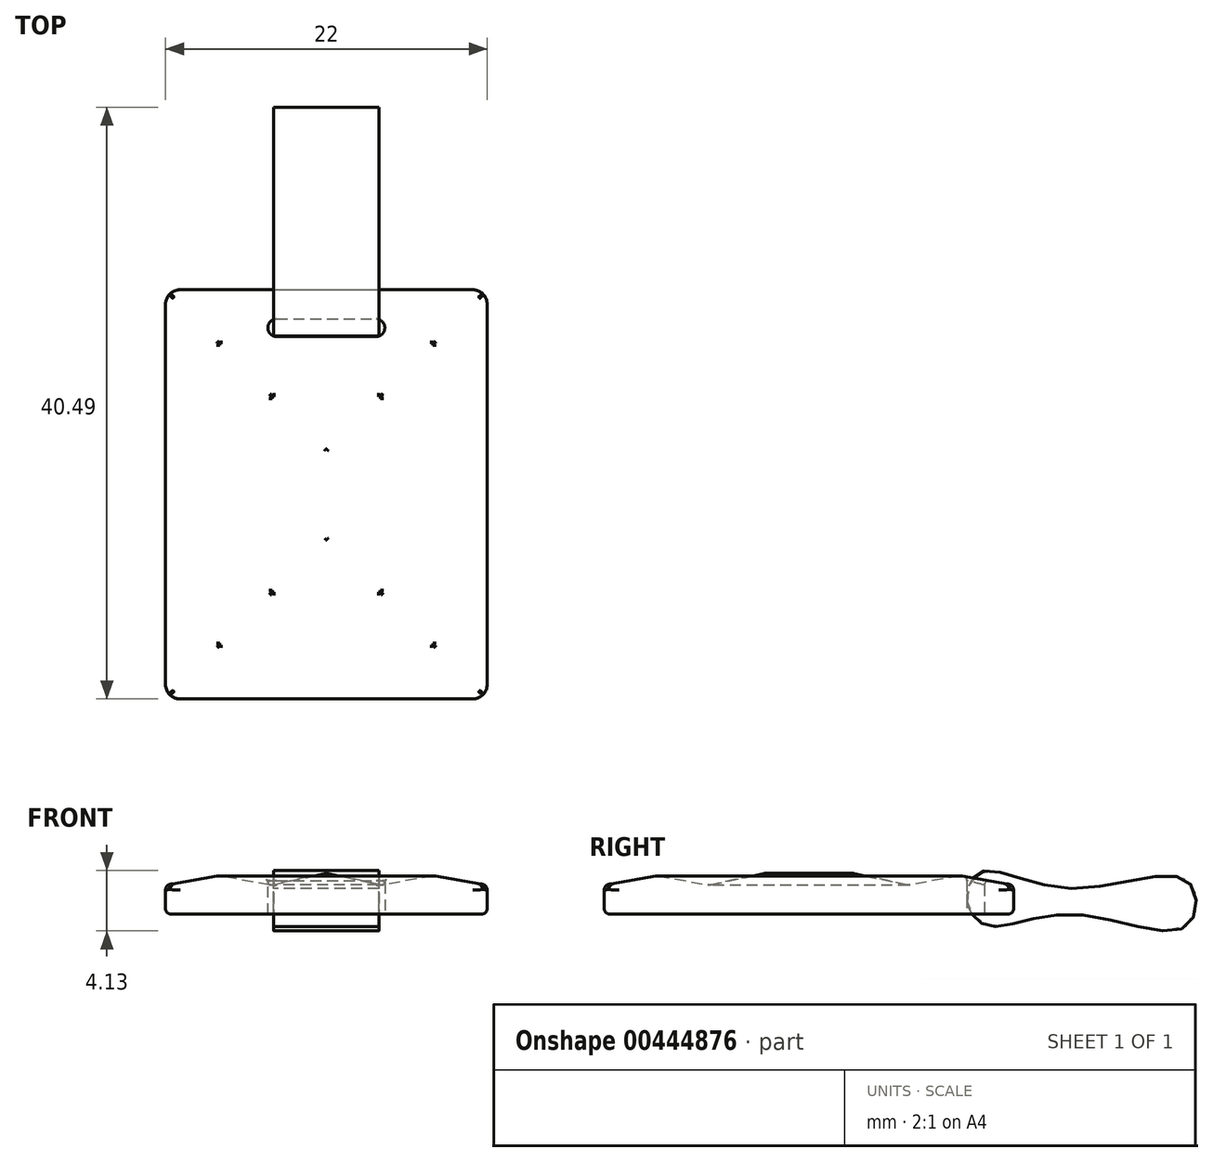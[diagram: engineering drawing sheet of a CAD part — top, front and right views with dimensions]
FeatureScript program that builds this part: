
annotation { "Feature Type Name" : "Feature", "Feature Type Description" : "" }
export const myFeature = defineFeature(function(context is Context, id is Id, definition is map)
    precondition{}
    {
        {
            var Q0;
            Q0=qCreatedBy(makeId("Top.planeOp"),FACE);
            var sketch = newSketch(context, id + "F0", { "sketchPlane" : qUnion([Q0])});
            skLineSegment(sketch, "E0.bottom", {"start": v(-11, 14) * mm, "end": v(11, 14) * mm});
            skLineSegment(sketch, "E0.top", {"start": v(-11, -14) * mm, "end": v(11, -14) * mm});
            skLineSegment(sketch, "E0.left", {"start": v(-11, 14) * mm, "end": v(-11, -14) * mm});
            skLineSegment(sketch, "E0.right", {"start": v(11, 14) * mm, "end": v(11, -14) * mm});
            skPoint(sketch, "E0.middle", {"position": v(0, 0) * mm});
            skSolve(sketch);
        }
        {
            var Q0;
            Q0 = qSketchRegion(id + "F0", true);
            extrude(context, id + "F1", {"entities" : qUnion([Q0]), "depth" : 2 * mm});
        }
        {
            var Q0;
            Q0=makeQuery(id+"F1.opExtrude","CAP_FACE",FACE,{"disambiguationData":[OSD([sQuery(id+"F0.wireOp",EDGE,"E0.bottom"),sQuery(id+"F0.wireOp",EDGE,"E0.top"),sQuery(id+"F0.wireOp",EDGE,"E0.left"),sQuery(id+"F0.wireOp",EDGE,"E0.right")])],"isStart":false});
            var sketch = newSketch(context, id + "F2", { "sketchPlane" : qUnion([Q0])});
            skLineSegment(sketch, "E1.bottom", {"start": v(-3.8, 6.8) * mm, "end": v(3.8, 6.8) * mm});
            skLineSegment(sketch, "E1.top", {"start": v(-3.8, -6.8) * mm, "end": v(3.8, -6.8) * mm});
            skLineSegment(sketch, "E1.left", {"start": v(-3.8, 6.8) * mm, "end": v(-3.8, -6.8) * mm});
            skLineSegment(sketch, "E1.right", {"start": v(3.8, 6.8) * mm, "end": v(3.8, -6.8) * mm});
            skPoint(sketch, "E1.middle", {"position": v(0, 0) * mm});
            skSolve(sketch);
        }
        {
            var Q0;
            Q0=makeQuery(id+"F2.imprint","IMPRINT",FACE,{"disambiguationData":[TD([[makeQuery(id+"F2.imprint","IMPRINT",EDGE,{"derivedFrom":sQuery(id+"F2.wireOp",EDGE,"E1.bottom")}),1.0]])]});
            extrude(context, id + "F3", {"entities" : qUnion([Q0]), "operationType" : NewBodyOperationType.ADD, "depth" : 25 * mm, "hasDraft" : true, "draftAngle" : 80 * degree, "draftPullDirection" : true});
        }
        {
            var Q0;
            Q0=makeQuery(id+"F1.opExtrude","CAP_FACE",FACE,{"disambiguationData":[OSD([sQuery(id+"F0.wireOp",EDGE,"E0.bottom"),sQuery(id+"F0.wireOp",EDGE,"E0.top"),sQuery(id+"F0.wireOp",EDGE,"E0.left"),sQuery(id+"F0.wireOp",EDGE,"E0.right")])],"isStart":false});
            extrude(context, id + "F4", {"entities" : qUnion([Q0]), "operationType" : NewBodyOperationType.ADD, "depth" : 25 * mm, "hasDraft" : true, "draftAngle" : 78 * degree, "draftPullDirection" : true});
        }
        {
            var Q0;
            Q0=makeQuery(id+"F1.opExtrude","SWEPT_EDGE",EDGE,{"disambiguationData":[OSD([sQuery(id+"F0.wireOp",EDGE,"E0.bottom"),sQuery(id+"F0.wireOp",EDGE,"E0.left")])]});
            var Q1;
            Q1=makeQuery(id+"F1.opExtrude","SWEPT_EDGE",EDGE,{"disambiguationData":[OSD([sQuery(id+"F0.wireOp",EDGE,"E0.top"),sQuery(id+"F0.wireOp",EDGE,"E0.left")])]});
            var Q2;
            Q2=makeQuery(id+"F1.opExtrude","SWEPT_EDGE",EDGE,{"disambiguationData":[OSD([sQuery(id+"F0.wireOp",EDGE,"E0.top"),sQuery(id+"F0.wireOp",EDGE,"E0.right")])]});
            var Q3;
            Q3=makeQuery(id+"F1.opExtrude","SWEPT_EDGE",EDGE,{"disambiguationData":[OSD([sQuery(id+"F0.wireOp",EDGE,"E0.bottom"),sQuery(id+"F0.wireOp",EDGE,"E0.right")])]});
            fillet(context, id + "F5", {"entities" : qUnion([Q0, Q1, Q2, Q3]), "radius" : 1 * mm, "tangentPropagation" : true, "allowEdgeOverflow" : false});
        }
        {
            var Q0;
            Q0=makeQuery(id+"F3.opExtrude","SWEPT_EDGE",EDGE,{"disambiguationData":[OSD([sQuery(id+"F0.wireOp",EDGE,"E0.bottom"),sQuery(id+"F0.wireOp",EDGE,"E0.left")])]});
            var Q1;
            Q1=makeQuery(id+"F3.opExtrude","SWEPT_EDGE",EDGE,{"disambiguationData":[OSD([sQuery(id+"F2.wireOp",EDGE,"E1.bottom"),sQuery(id+"F2.wireOp",EDGE,"E1.left")])]});
            var Q2;
            Q2=makeQuery(id+"F4.opExtrude","SWEPT_EDGE",EDGE,{"disambiguationData":[OSD([sQuery(id+"F2.wireOp",EDGE,"E1.bottom"),sQuery(id+"F2.wireOp",EDGE,"E1.left")])]});
            var Q3;
            Q3=makeQuery(id+"F4.opExtrude","SWEPT_EDGE",EDGE,{"disambiguationData":[OSD([sQuery(id+"F2.wireOp",EDGE,"E1.top"),sQuery(id+"F2.wireOp",EDGE,"E1.right")])]});
            var Q4;
            Q4=makeQuery(id+"F3.opExtrude","SWEPT_EDGE",EDGE,{"disambiguationData":[OSD([sQuery(id+"F2.wireOp",EDGE,"E1.top"),sQuery(id+"F2.wireOp",EDGE,"E1.right")])]});
            var Q5;
            Q5=makeQuery(id+"F3.opExtrude","SWEPT_EDGE",EDGE,{"disambiguationData":[OSD([sQuery(id+"F0.wireOp",EDGE,"E0.top"),sQuery(id+"F0.wireOp",EDGE,"E0.right")])]});
            var Q6;
            Q6=makeQuery(id+"F4.opExtrude","SWEPT_EDGE",EDGE,{"disambiguationData":[OSD([sQuery(id+"F2.wireOp",EDGE,"E1.top"),sQuery(id+"F2.wireOp",EDGE,"E1.left")])]});
            var Q7;
            Q7=makeQuery(id+"F4.opExtrude","SWEPT_EDGE",EDGE,{"disambiguationData":[OSD([sQuery(id+"F2.wireOp",EDGE,"E1.bottom"),sQuery(id+"F2.wireOp",EDGE,"E1.right")])]});
            var Q8;
            Q8=makeQuery(id+"F3.opExtrude","SWEPT_EDGE",EDGE,{"disambiguationData":[OSD([sQuery(id+"F2.wireOp",EDGE,"E1.top"),sQuery(id+"F2.wireOp",EDGE,"E1.left")])]});
            var Q9;
            Q9=makeQuery(id+"F3.opExtrude","SWEPT_EDGE",EDGE,{"disambiguationData":[OSD([sQuery(id+"F0.wireOp",EDGE,"E0.top"),sQuery(id+"F0.wireOp",EDGE,"E0.left")])]});
            var Q10;
            Q10=makeQuery(id+"F3.opExtrude","SWEPT_EDGE",EDGE,{"disambiguationData":[OSD([sQuery(id+"F2.wireOp",EDGE,"E1.bottom"),sQuery(id+"F2.wireOp",EDGE,"E1.right")])]});
            var Q11;
            Q11=makeQuery(id+"F3.opExtrude","SWEPT_EDGE",EDGE,{"disambiguationData":[OSD([sQuery(id+"F0.wireOp",EDGE,"E0.bottom"),sQuery(id+"F0.wireOp",EDGE,"E0.right")])]});
            fillet(context, id + "F6", {"entities" : qUnion([Q0, Q1, Q2, Q3, Q4, Q5, Q6, Q7, Q8, Q9, Q10, Q11]), "radius" : 0.6 * mm, "tangentPropagation" : true, "allowEdgeOverflow" : false});
        }
        {
            var Q0;
            Q0=makeQuery(id+"F3.*.draft.opDraft","TWEAK_EDGE",EDGE,{"derivedFrom":[makeQuery(id+"F3.opExtrude","SWEPT_FACE",FACE,{"disambiguationData":[OSD([sQuery(id+"F2.wireOp",EDGE,"E1.bottom")])]}),makeQuery(id+"F3.opExtrude","SWEPT_FACE",FACE,{"disambiguationData":[OSD([sQuery(id+"F0.wireOp",EDGE,"E0.bottom")])]})]});
            var Q1;
            {var subQ0=sQuery(id+"F2.wireOp",EDGE,"E1.bottom");Q1=makeQuery(id+"F4.boolean.opBoolean","MERGE",EDGE,{"derivedFrom":[makeQuery(id+"F3.opExtrude","CAP_EDGE",EDGE,{"disambiguationData":[OSD([subQ0])],"isStart":true}),makeQuery(id+"F4.opExtrude","CAP_EDGE",EDGE,{"disambiguationData":[OSD([subQ0])],"isStart":true})]});}
            var Q2;
            Q2=makeQuery(id+"F4.*.draft.opDraft","TWEAK_EDGE",EDGE,{"derivedFrom":[makeQuery(id+"F4.opExtrude","SWEPT_FACE",FACE,{"disambiguationData":[OSD([sQuery(id+"F2.wireOp",EDGE,"E1.left")])]}),makeQuery(id+"F4.opExtrude","SWEPT_FACE",FACE,{"disambiguationData":[OSD([sQuery(id+"F2.wireOp",EDGE,"E1.right")])]})]});
            fillet(context, id + "F7", {"entities" : qUnion([Q0, Q1, Q2]), "radius" : 0.6 * mm, "tangentPropagation" : true, "allowEdgeOverflow" : false});
        }
        {
            var Q0;
            {var subQ0=sQuery(id+"F0.wireOp",EDGE,"E0.top");Q0=makeQuery(id+"F3.boolean.opBoolean","MERGE",EDGE,{"derivedFrom":[makeQuery(id+"F1.opExtrude","CAP_EDGE",EDGE,{"disambiguationData":[OSD([subQ0])],"isStart":false}),makeQuery(id+"F3.opExtrude","CAP_EDGE",EDGE,{"disambiguationData":[OSD([subQ0])],"isStart":true})]});}
            var Q1;
            Q1=makeQuery(id+"F1.opExtrude","CAP_EDGE",EDGE,{"disambiguationData":[OSD([sQuery(id+"F0.wireOp",EDGE,"E0.top")])],"isStart":true});
            fillet(context, id + "F8", {"entities" : qUnion([Q0, Q1]), "radius" : 0.4 * mm, "tangentPropagation" : true, "allowEdgeOverflow" : false});
        }
        {
            var Q0;
            Q0=qCreatedBy(makeId("Top.planeOp"),FACE);
            var sketch = newSketch(context, id + "F9", { "sketchPlane" : qUnion([Q0])});
            skLineSegment(sketch, "E2.bottom", {"start": v(-4, 10.8) * mm, "end": v(4, 10.8) * mm});
            skLineSegment(sketch, "E2.top", {"start": v(-4, 12) * mm, "end": v(4, 12) * mm});
            skLineSegment(sketch, "E2.left", {"start": v(-4, 10.8) * mm, "end": v(-4, 12) * mm});
            skLineSegment(sketch, "E2.right", {"start": v(4, 10.8) * mm, "end": v(4, 12) * mm});
            skPoint(sketch, "E2.middle", {"position": v(0, 11.4) * mm});
            skSolve(sketch);
        }
        {
            var Q0;
            Q0 = qSketchRegion(id + "F9", true);
            extrude(context, id + "F10", {"entities" : qUnion([Q0]), "operationType" : NewBodyOperationType.REMOVE, "depth" : 25 * mm});
        }
        {
            var Q0;
            Q0=makeQuery(id+"F10.boolean.opBoolean","COPY",EDGE,{"derivedFrom":makeQuery(id+"F10.opExtrude","SWEPT_EDGE",EDGE,{"disambiguationData":[OSD([sQuery(id+"F9.wireOp",EDGE,"E2.top"),sQuery(id+"F9.wireOp",EDGE,"E2.left")])]})});
            var Q1;
            Q1=makeQuery(id+"F10.boolean.opBoolean","COPY",EDGE,{"derivedFrom":makeQuery(id+"F10.opExtrude","SWEPT_EDGE",EDGE,{"disambiguationData":[OSD([sQuery(id+"F9.wireOp",EDGE,"E2.bottom"),sQuery(id+"F9.wireOp",EDGE,"E2.left")])]})});
            var Q2;
            Q2=makeQuery(id+"F10.boolean.opBoolean","COPY",EDGE,{"derivedFrom":makeQuery(id+"F10.opExtrude","SWEPT_EDGE",EDGE,{"disambiguationData":[OSD([sQuery(id+"F9.wireOp",EDGE,"E2.top"),sQuery(id+"F9.wireOp",EDGE,"E2.right")])]})});
            var Q3;
            Q3=makeQuery(id+"F10.boolean.opBoolean","COPY",EDGE,{"derivedFrom":makeQuery(id+"F10.opExtrude","SWEPT_EDGE",EDGE,{"disambiguationData":[OSD([sQuery(id+"F9.wireOp",EDGE,"E2.bottom"),sQuery(id+"F9.wireOp",EDGE,"E2.right")])]})});
            fillet(context, id + "F11", {"entities" : qUnion([Q0, Q1, Q2, Q3]), "radius" : 0.6 * mm, "tangentPropagation" : true, "allowEdgeOverflow" : false});
        }
        {
            var Q0;
            Q0=qCreatedBy(makeId("Right.planeOp"),FACE);
            var sketch = newSketch(context, id + "F12", { "sketchPlane" : qUnion([Q0])});
            skFitSpline(sketch, "E3", {"points": [v(10.86, 0.8) * mm, v(11.77, 2.9) * mm, v(17.83, 1.78) * mm, v(25.9, 2.27) * mm, v(25.8, -0.82) * mm, v(18.02, 0) * mm, v(12.33, -0.8) * mm, v(10.86, 0.8) * mm]});
            skFitSpline(sketch, "E4.0", {"points": [v(11.51, 0.62) * mm, v(11.45, 0.9) * mm, v(11.43, 1.2) * mm, v(11.46, 1.51) * mm, v(11.54, 1.8) * mm, v(11.65, 2.05) * mm, v(11.8, 2.23) * mm, v(11.91, 2.31) * mm, v(12, 2.35) * mm, v(12.13, 2.38) * mm, v(12.36, 2.4) * mm, v(12.74, 2.35) * mm, v(13.2, 2.23) * mm, v(13.74, 2.07) * mm, v(14.53, 1.82) * mm, v(15.42, 1.55) * mm, v(16.41, 1.33) * mm, v(17.2, 1.2) * mm, v(18.02, 1.16) * mm, v(18.86, 1.19) * mm, v(19.69, 1.27) * mm, v(20.79, 1.44) * mm, v(22.12, 1.7) * mm, v(23.31, 1.94) * mm, v(24.14, 2.03) * mm, v(24.67, 2.05) * mm, v(25.1, 2) * mm, v(25.35, 1.91) * mm, v(25.49, 1.83) * mm, v(25.6, 1.73) * mm, v(25.73, 1.54) * mm, v(25.85, 1.23) * mm, v(25.9, 0.86) * mm, v(25.88, 0.48) * mm, v(25.79, 0.13) * mm, v(25.66, -0.1) * mm, v(25.54, -0.25) * mm, v(25.45, -0.33) * mm, v(25.35, -0.4) * mm, v(25.17, -0.47) * mm, v(24.88, -0.54) * mm, v(24.4, -0.55) * mm, v(23.84, -0.5) * mm, v(23.2, -0.39) * mm, v(22.28, -0.19) * mm, v(21.02, 0.13) * mm, v(19.7, 0.42) * mm, v(18.64, 0.57) * mm, v(17.85, 0.62) * mm, v(17.09, 0.59) * mm, v(16.13, 0.48) * mm, v(15.03, 0.24) * mm, v(14.1, 0) * mm, v(13.44, -0.15) * mm, v(13.02, -0.22) * mm, v(12.72, -0.24) * mm, v(12.52, -0.22) * mm, v(12.35, -0.2) * mm, v(12.15, -0.13) * mm, v(11.88, 0.04) * mm, v(11.66, 0.3) * mm, v(11.51, 0.62) * mm, v(11.45, 0.9) * mm, v(11.43, 1.2) * mm, v(11.51, 0.62) * mm]});
            skSolve(sketch);
        }
        {
            var Q0;
            Q0 = qSketchRegion(id + "F12", true);
            extrude(context, id + "F13", {"entities" : qUnion([Q0]), "depth" : 3.6 * mm, "hasSecondDirection" : true, "secondDirectionOppositeDirection" : true, "secondDirectionDepth" : 3.6 * mm});
        }
        {
            var Q0;
            Q0=makeQuery(id+"F10.boolean.opBoolean","INTERSECT",EDGE,{"derivedFrom":[makeQuery(id+"F3.opExtrude","SWEPT_FACE",FACE,{"disambiguationData":[OSD([sQuery(id+"F0.wireOp",EDGE,"E0.bottom")])]}),makeQuery(id+"F10.opExtrude","SWEPT_FACE",FACE,{"disambiguationData":[OSD([sQuery(id+"F9.wireOp",EDGE,"E2.bottom")])]})]});
            var Q1;
            Q1=makeQuery(id+"F11.opFillet","BLEND_EDGE",EDGE,{"blendedFrom":[makeQuery(id+"F10.boolean.opBoolean","COPY",EDGE,{"derivedFrom":makeQuery(id+"F10.opExtrude","SWEPT_EDGE",EDGE,{"disambiguationData":[OSD([sQuery(id+"F9.wireOp",EDGE,"E2.top"),sQuery(id+"F9.wireOp",EDGE,"E2.left")])]})}),makeQuery(id+"F1.opExtrude","CAP_FACE",FACE,{"disambiguationData":[OSD([sQuery(id+"F0.wireOp",EDGE,"E0.bottom"),sQuery(id+"F0.wireOp",EDGE,"E0.top"),sQuery(id+"F0.wireOp",EDGE,"E0.left"),sQuery(id+"F0.wireOp",EDGE,"E0.right")])],"isStart":true})],"blendedInto":[makeQuery(id+"F1.opExtrude","CAP_FACE",FACE,{"disambiguationData":[OSD([sQuery(id+"F0.wireOp",EDGE,"E0.bottom"),sQuery(id+"F0.wireOp",EDGE,"E0.top"),sQuery(id+"F0.wireOp",EDGE,"E0.left"),sQuery(id+"F0.wireOp",EDGE,"E0.right")])],"isStart":true})]});
            fillet(context, id + "F14", {"entities" : qUnion([Q0, Q1]), "radius" : 0.3 * mm, "tangentPropagation" : true, "allowEdgeOverflow" : false});
        }
    });
